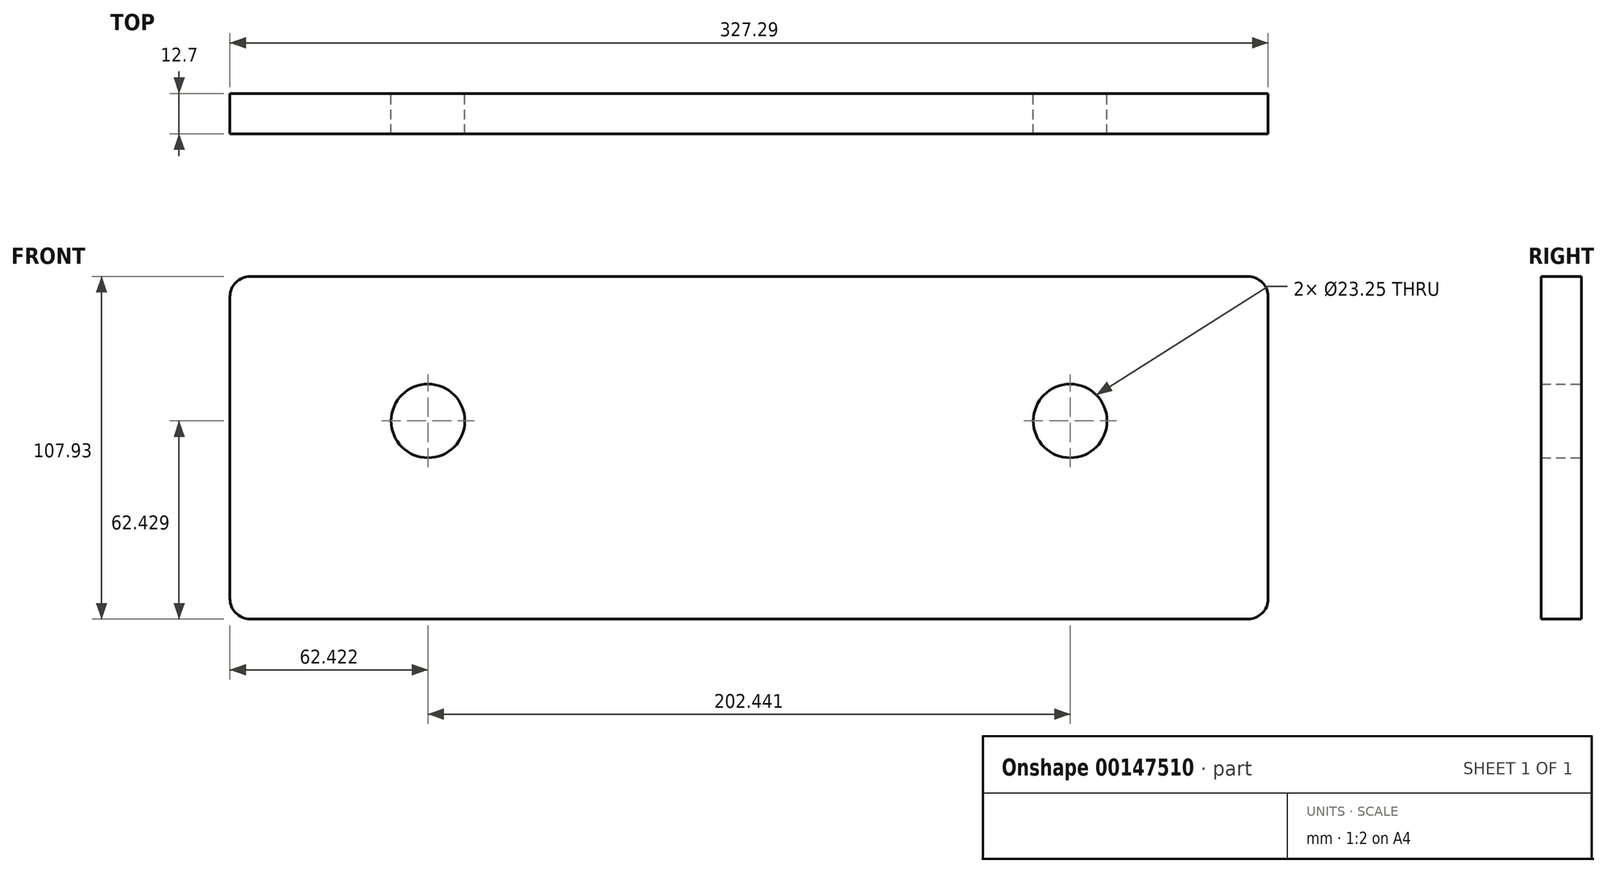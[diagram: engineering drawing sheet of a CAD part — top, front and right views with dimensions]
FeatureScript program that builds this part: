
annotation { "Feature Type Name" : "Feature", "Feature Type Description" : "" }
export const myFeature = defineFeature(function(context is Context, id is Id, definition is map)
    precondition{}
    {
        {
            var Q0;
            Q0=qCreatedBy(makeId("Front.planeOp"),FACE);
            var sketch = newSketch(context, id + "F0", { "sketchPlane" : qUnion([Q0])});
            skLineSegment(sketch, "E0.bottom", {"start": v(-143.2, 66.27) * mm, "end": v(184.1, 66.27) * mm});
            skLineSegment(sketch, "E0.top", {"start": v(-143.2, -41.66) * mm, "end": v(184.1, -41.66) * mm});
            skLineSegment(sketch, "E0.left", {"start": v(-143.2, 66.27) * mm, "end": v(-143.2, -41.66) * mm});
            skLineSegment(sketch, "E0.right", {"start": v(184.1, 66.27) * mm, "end": v(184.1, -41.66) * mm});
            skCircle(sketch, "E1", {"center": v(-80.77, 20.77) * mm, "radius": 11.62 * mm});
            skCircle(sketch, "E2", {"center": v(121.67, 20.77) * mm, "radius": 11.62 * mm});
            skSolve(sketch);
        }
        {
            var Q0;
            Q0 = qSketchRegion(id + "F0", true);
            extrude(context, id + "F1", {"entities" : qUnion([Q0]), "depth" : 12.7 * mm});
        }
        {
            var Q0;
            Q0=makeQuery(id+"F1.opExtrude","SWEPT_EDGE",EDGE,{"disambiguationData":[OSD([sQuery(id+"F0.wireOp",EDGE,"E0.bottom"),sQuery(id+"F0.wireOp",EDGE,"E0.left")])]});
            var Q1;
            Q1=makeQuery(id+"F1.opExtrude","SWEPT_EDGE",EDGE,{"disambiguationData":[OSD([sQuery(id+"F0.wireOp",EDGE,"E0.top"),sQuery(id+"F0.wireOp",EDGE,"E0.left")])]});
            var Q2;
            Q2=makeQuery(id+"F1.opExtrude","SWEPT_EDGE",EDGE,{"disambiguationData":[OSD([sQuery(id+"F0.wireOp",EDGE,"E0.top"),sQuery(id+"F0.wireOp",EDGE,"E0.right")])]});
            var Q3;
            Q3=makeQuery(id+"F1.opExtrude","SWEPT_EDGE",EDGE,{"disambiguationData":[OSD([sQuery(id+"F0.wireOp",EDGE,"E0.bottom"),sQuery(id+"F0.wireOp",EDGE,"E0.right")])]});
            fillet(context, id + "F2", {"entities" : qUnion([Q0, Q1, Q2, Q3]), "radius" : 6.35 * mm, "tangentPropagation" : true, "allowEdgeOverflow" : false});
        }
    });
